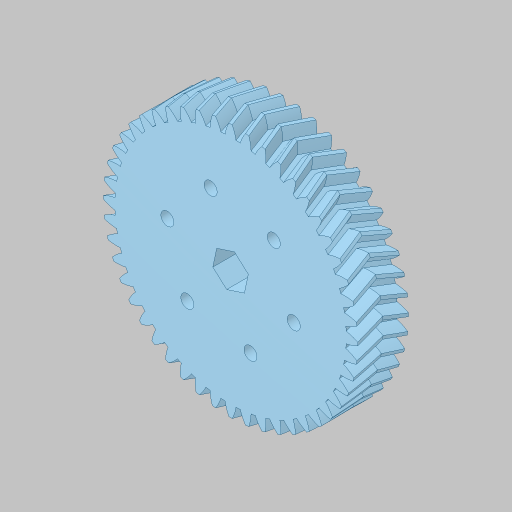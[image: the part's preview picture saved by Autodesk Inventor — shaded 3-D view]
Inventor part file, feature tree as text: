
AUTODESK INVENTOR PART (.ipt)
format: ipt  version: 2023.5 (Build 275446000, 446)  size: 1,337,856 bytes
history: native  units: in
note: dims shown in document units (in); Inventor stores cm internally (conversion verified against a paired STEP export)
features: sketch x2, projected_geometry x2, extrude x1, hole x1, other x1
ambient origin geometry x8: Origin, YZ Plane, XZ Plane, XY Plane, X Axis, Y Axis, Z Axis, Center Point
bodies: Solid1 (feature_tree)
feature tree (7):
  extrude  "Extrusion1"  Depth=1.0in TaperAngle=0.0deg
  hole  "Hole1"  [1 undecoded]
  sketch  "Sketch1"  dims[d0=0.5in d1=1.0in d2=0.0in]
  sketch  "Sketch2"  dims[d3=3.7597in d4=2.0in d9=2.3622in d11=360.0deg d13=0.201in d14=0.75in d15=0.385in d16=0.25in d17=0.5635in d18=1.0in d19=0.8108in]
  other  "Helical 2M 48T"
  projected_geometry  "Project Cut Edges1"
  projected_geometry  "Project Cut Edges2"
note: 1 required parameter value undecoded (feature->parameter linkage not recoverable at this tier; creation-order binding heuristic only, values carry confidence <= 0.55)
